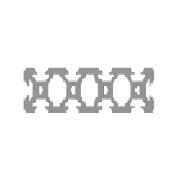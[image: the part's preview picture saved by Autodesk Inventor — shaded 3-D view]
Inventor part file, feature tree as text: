
AUTODESK INVENTOR PART (.ipt)
format: ipt  version: 2013 (Build 170138000, 138)  size: 279,040 bytes
history: native  units: mm
features: other x4, sketch x2, plane x1
ambient origin geometry x8: Origin, YZ Plane, XZ Plane, XY Plane, X Axis, Y Axis, Z Axis, Center Point
bodies: Solid1 (feature_tree), Body (feature_tree)
feature tree (7):
  other  "Driven Length"
  other  "Frame Generator"
  other  "Start Plane"
  other  "End Plane"
  sketch  "Sketch10"  dims[d0=10.0mm]
  plane  "Work Plane7"
  sketch  "Sketch11"  dims[d1=10.0mm d2=10.0mm d3=4.2mm d4=1.5mm d5=45.0deg d6=1.64mm d7=1.8mm d8=10.0mm d9=2.84mm d11=135.0deg d12=1.96mm d13=5.68mm d14=2.0mm d17=-0.0mm d18=475.0mm d19=0.13mm d20=0.0mm d29=90.0deg d22=475.0mm]
